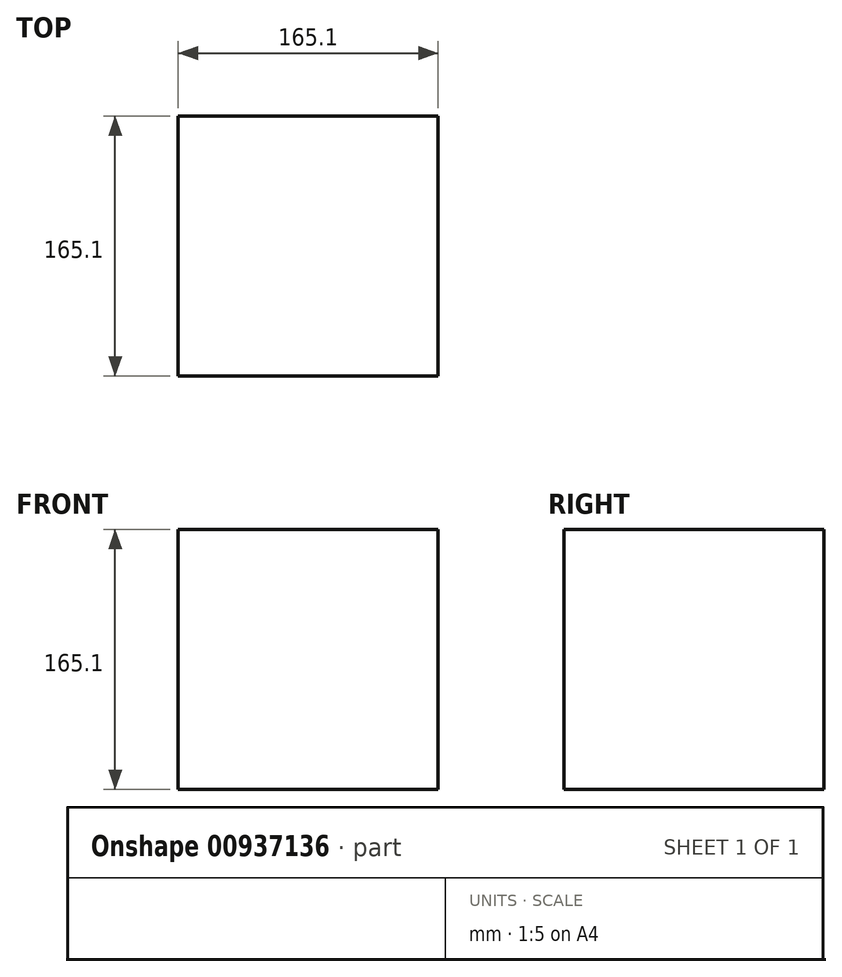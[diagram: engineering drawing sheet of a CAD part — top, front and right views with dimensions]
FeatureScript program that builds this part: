
annotation { "Feature Type Name" : "Feature", "Feature Type Description" : "" }
export const myFeature = defineFeature(function(context is Context, id is Id, definition is map)
    precondition{}
    {
        {
            assignVariable(context, id + "F0", {"name" : "size", "anyValue" : 165.1 * mm});
        }
        {
            var Q0;
            Q0=qCreatedBy(makeId("Front.planeOp"),FACE);
            var sketch = newSketch(context, id + "F1", { "sketchPlane" : qUnion([Q0])});
            skLineSegment(sketch, "E0.bottom", {"start": v(-82.55, 82.55) * mm, "end": v(82.55, 82.55) * mm});
            skLineSegment(sketch, "E0.top", {"start": v(-82.55, -82.55) * mm, "end": v(82.55, -82.55) * mm});
            skLineSegment(sketch, "E0.left", {"start": v(-82.55, 82.55) * mm, "end": v(-82.55, -82.55) * mm});
            skLineSegment(sketch, "E0.right", {"start": v(82.55, 82.55) * mm, "end": v(82.55, -82.55) * mm});
            skPoint(sketch, "E0.middle", {"position": v(0, 0) * mm});
            skSolve(sketch);
        }
        {
            var Q0;
            Q0=makeQuery(id+"F1.imprint","IMPRINT",FACE,{"disambiguationData":[TD([[makeQuery(id+"F1.imprint","IMPRINT",EDGE,{"derivedFrom":sQuery(id+"F1.wireOp",EDGE,"E0.bottom")}),-1.0]])]});
            extrude(context, id + "F2", {"entities" : qUnion([Q0]), "depth" : getVariable(context, 'size'), "offsetDistance" : 25.4 * mm});
        }
    });
